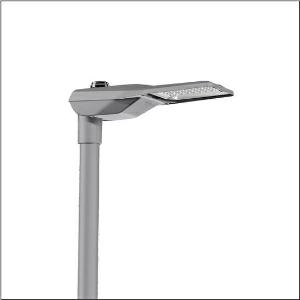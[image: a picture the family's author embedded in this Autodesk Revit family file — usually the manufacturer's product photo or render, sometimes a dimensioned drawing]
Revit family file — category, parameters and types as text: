
# Revit family: streetlight_sl_21_mini___st1_0a_5xe6d67n08jb_11ba
name_source: partatom
category: Lighting Fixtures
units: mm (PartAtom-declared; Revit-internal decimal feet)

## family parameters
Cut with Voids When Loaded = No
Host = Face
Light Source = No
Part Type = Normal
Room Calculation Point = No
Round Connector Dimension = Use Diameter
Shared = No

## types (1)
- --- (1 x LED, 11500 lm, 87.3 W, 2700K)
    Apparent Load = 87 VA
    CIE Flux Codes = 40 73 97 100 100
    Color Rendering = 70
    Color Temperature = 2700K
    Default Elevation = 1800 mm
    Description = Streetlight SL 21 mini, mast luminaire, primary light control with lens, of PMMA, primary optical cover: cover, of toughened safety glass, transparent, light distribution: ST1.0a, light emission: direct distribution, primary light characteristic: asymmetric, installation type: side-entry, LED, 3G 2.5mm², High Power LED, rated luminous flux: 11.500lm, luminous efficacy: 132lm/W, light colour: 727, colour temperature: 2700K, control: overheat protection, pre-setting: linear dimming characteristic, constant luminous flux control, time-dependent luminous flux control, flexible luminous flux parameterisation, mains connection: 230..240V, AC, 50/60Hz, connection cable pre-assembled, cable length: 10,5m, wiring characteristics: H05VV-F, start of lifetime: 87W, end of service life: 90W, reduction: 40W, luminaire housing, of diecast aluminium (EN AC-44300), powder-coated, Siteco® metallic grey (DB 702S), corrosivity category C5 mid according to DIN EN ISO 12944, multi-level sealing system, sealing non-destructively replaceable, inclination adjustable: 0°, 5°, 10°, 15°, length: 628mm, width: 235mm, height: 110mm, spigot size: 42mm (side-entry), protection rating (complete): IP66, insulation class (complete): insulation class I (protective earthing), certification: CE, ENEC, ENEC+, VDE, impact resistance: IK09, permissible operating ambient temperature for outdoor applications: -40..+50°C, standard-compliant lighting for roads and squares, packaging unit: 1 piece

Light Distribution: ST1.0a
    Height = 110 mm
    Lamp = 1 x LED
    Lamp Light Flux = 11500 lm
    Lamp Power = 87.3 W
    Lamp count = 1
    Length = 625 mm
    Luminous efficacy = 132 lm/W
    Manufacturer = Siteco
    ModVariant = No
    Model = 5XE6D67N08JB
    Number of Poles = 1
    OnlyDefault = Yes
    Power Factor = 1
    Product Name = Streetlight SL 21 mini | ST1.0a
    Product group = mast luminaire | pylon top
    ProductGroupID = 6100
    Protection Class = Protection class I
    Protection Degree = IP 66
    RLX_Detail_Level = 1
    RLX_Emergency_Light_Flux = 0 lm
    RLX_Emergency_Type = 0
    RLX_Emergency_Type_DB = No
    RlxData = <blob elided: 92469 chars, md5=4de525d7>
    Socket = socket
    Standby Power = 0 W
    System Light Flux = 11500 lm
    System Power = 87 W
    Type Comments = factory setting: luminous flux: 100 % | dim-lin: 254 | 915 mA
    Type Image = l_1294379.jpg
    URL = http://relux.com
    VarID = @adj_105045
    Voltage = 0 V
    Weight = 0.00 kg
    Width = 234 mm

## geometry (parser evidence)
native form markers: Blend x4, Sweep x10
no freeform markers — native parametric forms only
